# Revit family: LAMP_KOMBIC 100 SURFACE 2500 CRI80 OPAL DALI
name_source: partatom
category: Luminarias
revit_build: Autodesk Revit 2018 (Build: 20190510_1515(x64)
units: mm (PartAtom-declared; Revit-internal decimal feet)

## family parameters
Anfitrión = Cara
Compartido = No
Corte con vacíos al cargar = No
Cota de conector redondo = Diámetro de uso
Origen de luz = Sí
Punto de cálculo de habitación = No
Tipo de pieza = Normal

## types (12) — shared parameters
CRI = 80
Cambio de temperatura de color de luz atenuada = <Ninguno>
Diameter = 100 mm  [stored 0.328084 ft]
Elevación por defecto = 1219 mm
Fabricante = LAMP
Filtro de color = 16777215
Gear = Electronic
Height = 180 mm  [stored 0.590551 ft]
IEE = A+
Installation instructions = https://www.lamp.es
Insulation class = I
LED Lifetime = 50.000 L80 B10
Lamp = COB LED
Last update = 26/07/2021
Luminaire type = Suspended
MacAdam = 3
Manufacturer URL = http://www.lamp.es
Manufacturer country = Spain
Manufacturer name = LAMP
Material cable suspension = LAMP_Acero genérico
Material difusor = LAMP_PMMA Difusor Kombic
Model explanation = Possibility of chossing between surface or suspended within the model
Plum = 20 W
Power = 17 W
Power Supply = 220-240V 50/60Hz
Product URL = https://www.lamp.es
Product datasheet = http://www.lamp.es
Protection rating = IP40
Type = COB PHILIPS
Weight = 0.72 kg
Ángulo de inclinación = -90.00°

## per-type parameters (varying)
| type | Archivo de red fotométrica | Efficacy | Finish | Material cuerpo | Material floron | Material reflector | Modelo | Product code |
| 1867LM 3000K DALI M/B | K11SF2540OP830DMB.IES | 92 lm/W | Matte black RAL 9011 | LAMP_Plástico genérico NG | LAMP_Plástico genérico NG | LAMP_PC Reflector Kombic Metalizado Mate | K11SF2540OP830DMB | K11SF2540OP830DMB |
| 1867LM 3000K DALI M/W | K11SF2540OP830DMW.IES | 92 lm/W | Matte Traffic white RAL 9016 | LAMP_Plástico genérico BL | LAMP_Plástico genérico BL | LAMP_PC Reflector Kombic Metalizado Mate | K11SF2540OP830DMW | K11SF2540OP830DMW |
| 1951LM 3000K DALI W/B | K11SF2540OP830DWB.IES | 96 lm/W | Matte black RAL 9011 | LAMP_Plástico genérico NG | LAMP_Plástico genérico NG | LAMP_PC Reflector Kombic Blanco | K11SF2540OP830DWB | K11SF2540OP830DWB |
| 1951LM 3000K DALI W/W | K11SF2540OP830DWW.IES | 96 lm/W | Matte Traffic white RAL 9016 | LAMP_Plástico genérico BL | LAMP_Plástico genérico BL | LAMP_PC Reflector Kombic Blanco | K11SF2540OP830DWW | K11SF2540OP830DWW |
| 1959LM 3000K DALI BR/B | K11SF2540OP830DRB.IES | 96 lm/W | Matte black RAL 9011 | LAMP_Plástico genérico NG | LAMP_Plástico genérico NG | LAMP_PC Reflector Kombic Metalizado Brillante | K11SF2540OP830DRB | K11SF2540OP830DRB |
| 1959LM 3000K DALI BR/W | K11SF2540OP830DRW.IES | 96 lm/W | Matte Traffic white RAL 9016 | LAMP_Plástico genérico BL | LAMP_Plástico genérico BL | LAMP_PC Reflector Kombic Metalizado Brillante | K11SF2540OP830DRW | K11SF2540OP830DRW |
| 1978LM 4000K DALI M/B | K11SF2540OP840DMB.IES | 97 lm/W | Matte black RAL 9011 | LAMP_Plástico genérico NG | LAMP_Plástico genérico NG | LAMP_PC Reflector Kombic Metalizado Mate | K11SF2540OP840DMB | K11SF2540OP840DMB |
| 1978LM 4000K DALI M/W | K11SF2540OP840DMW.IES | 97 lm/W | Matte Traffic white RAL 9016 | LAMP_Plástico genérico BL | LAMP_Plástico genérico BL | LAMP_PC Reflector Kombic Metalizado Mate | K11SF2540OP840DMW | K11SF2540OP840DMW |
| 2067LM 4000K DALI W/B | K11SF2540OP840DWB.IES | 101 lm/W | Matte black RAL 9011 | LAMP_Plástico genérico NG | LAMP_Plástico genérico NG | LAMP_PC Reflector Kombic Blanco | K11SF2540OP840DWB | K11SF2540OP840DWB |
| 2067LM 4000K DALI W/W | K11SF2540OP840DWW.IES | 101 lm/W | Matte Traffic white RAL 9016 | LAMP_Plástico genérico BL | LAMP_Plástico genérico BL | LAMP_PC Reflector Kombic Blanco | K11SF2540OP840DWW | K11SF2540OP840DWW |
| 2075LM 4000K DALI BR/B | K11SF2540OP840DRB.IES | 102 lm/W | Matte black RAL 9011 | LAMP_Plástico genérico NG | LAMP_Plástico genérico NG | LAMP_PC Reflector Kombic Metalizado Brillante | K11SF2540OP840DRB | K11SF2540OP840DRB |
| 2075LM 4000K DALI BR/W | K11SF2540OP840DRW.IES | 102 lm/W | Matte Traffic white RAL 9016 | LAMP_Plástico genérico BL | LAMP_Plástico genérico BL | LAMP_PC Reflector Kombic Metalizado Brillante | K11SF2540OP840DRW | K11SF2540OP840DRW |

note: [stored X ft] marks values corroborated as IEEE doubles in the binary element streams (Revit-internal decimal feet)
